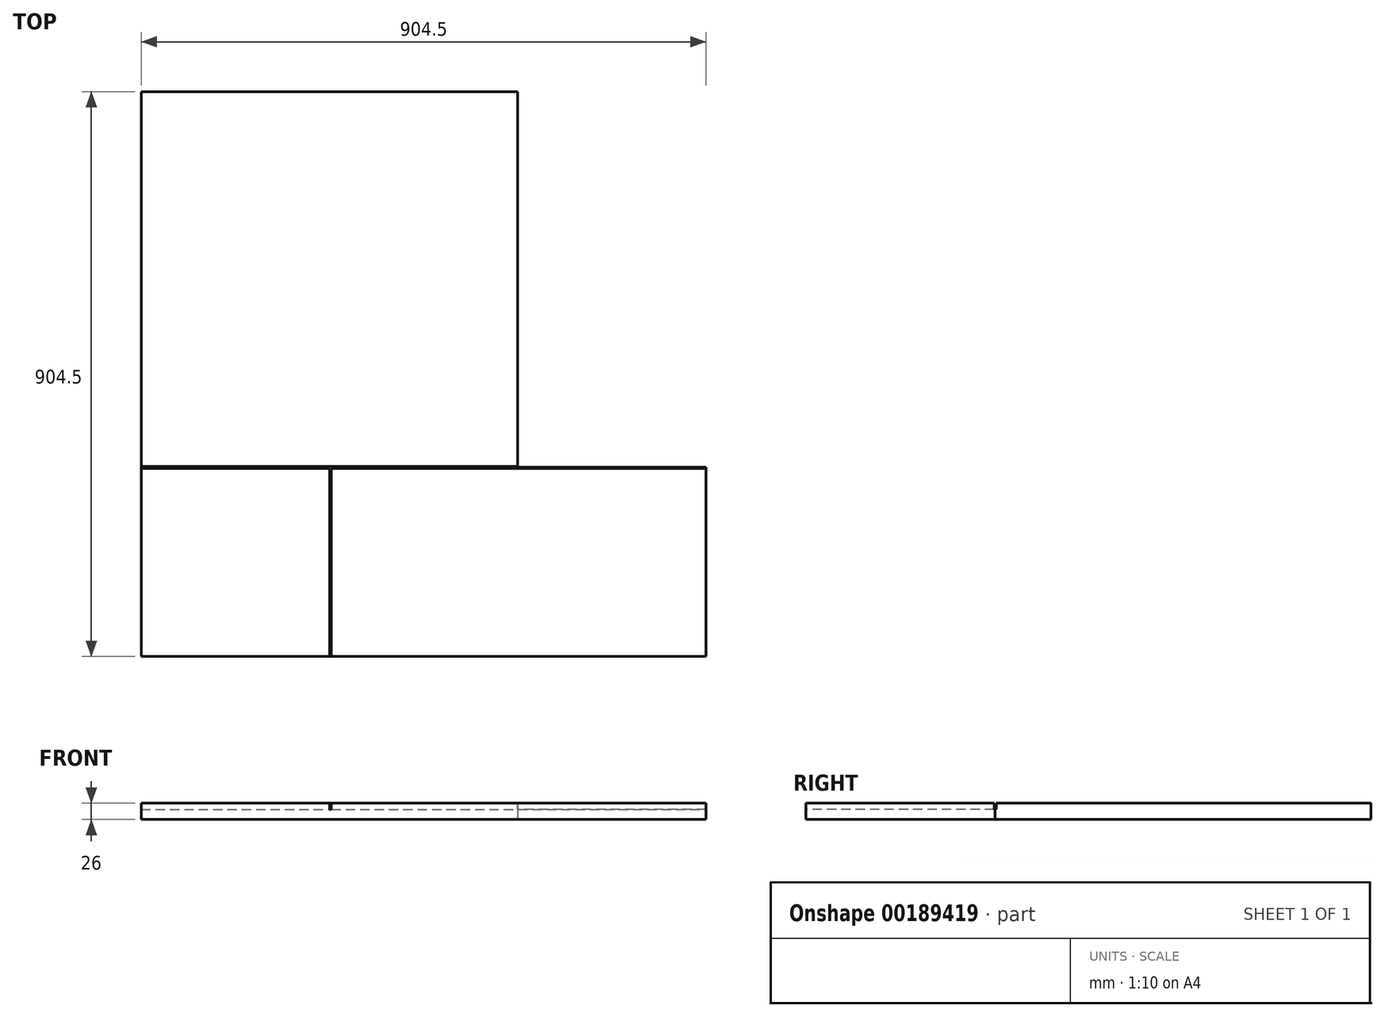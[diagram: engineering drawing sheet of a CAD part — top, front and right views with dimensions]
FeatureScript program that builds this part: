
annotation { "Feature Type Name" : "Feature", "Feature Type Description" : "" }
export const myFeature = defineFeature(function(context is Context, id is Id, definition is map)
    precondition{}
    {
        {
            var Q0;
            Q0=qCreatedBy(makeId("Top.planeOp"),FACE);
            var sketch = newSketch(context, id + "F0", { "sketchPlane" : qUnion([Q0])});
            skLineSegment(sketch, "E0", {"start": v(0, 0) * mm, "end": v(0, -904.5) * mm});
            skLineSegment(sketch, "E1", {"start": v(0, -904.5) * mm, "end": v(904.5, -904.5) * mm});
            skLineSegment(sketch, "E2", {"start": v(904.5, -904.5) * mm, "end": v(904.5, -601.5) * mm});
            skLineSegment(sketch, "E3", {"start": v(904.5, -601.5) * mm, "end": v(603, -601.5) * mm});
            skLineSegment(sketch, "E4", {"start": v(603, -601.5) * mm, "end": v(603, 0) * mm});
            skLineSegment(sketch, "E5", {"start": v(603, 0) * mm, "end": v(0, 0) * mm});
            skSolve(sketch);
        }
        {
            var Q0;
            Q0 = qSketchRegion(id + "F0", true);
            extrude(context, id + "F1", {"entities" : qUnion([Q0]), "depth" : 26 * mm});
        }
        {
            var Q0;
            Q0=makeQuery(id+"F1.opExtrude","CAP_FACE",FACE,{"disambiguationData":[OSD([sQuery(id+"F0.wireOp",EDGE,"E0"),sQuery(id+"F0.wireOp",EDGE,"E1"),sQuery(id+"F0.wireOp",EDGE,"E2"),sQuery(id+"F0.wireOp",EDGE,"E3"),sQuery(id+"F0.wireOp",EDGE,"E4"),sQuery(id+"F0.wireOp",EDGE,"E5")])],"isStart":false});
            var sketch = newSketch(context, id + "F2", { "sketchPlane" : qUnion([Q0])});
            skLineSegment(sketch, "E6.bottom", {"start": v(0, -603) * mm, "end": v(904.5, -603) * mm});
            skLineSegment(sketch, "E6.top", {"start": v(0, -600) * mm, "end": v(904.5, -600) * mm});
            skLineSegment(sketch, "E6.left", {"start": v(0, -603) * mm, "end": v(0, -600) * mm});
            skLineSegment(sketch, "E6.right", {"start": v(904.5, -603) * mm, "end": v(904.5, -600) * mm});
            skLineSegment(sketch, "E7.bottom", {"start": v(301.5, -603) * mm, "end": v(304.5, -603) * mm});
            skLineSegment(sketch, "E7.top", {"start": v(301.5, -904.5) * mm, "end": v(304.5, -904.5) * mm});
            skLineSegment(sketch, "E7.left", {"start": v(301.5, -603) * mm, "end": v(301.5, -904.5) * mm});
            skLineSegment(sketch, "E7.right", {"start": v(304.5, -603) * mm, "end": v(304.5, -904.5) * mm});
            skSolve(sketch);
        }
        {
            var Q0;
            Q0 = qSketchRegion(id + "F2", true);
            extrude(context, id + "F3", {"entities" : qUnion([Q0]), "operationType" : NewBodyOperationType.REMOVE, "oppositeDirection" : true, "depth" : 10 * mm});
        }
    });
